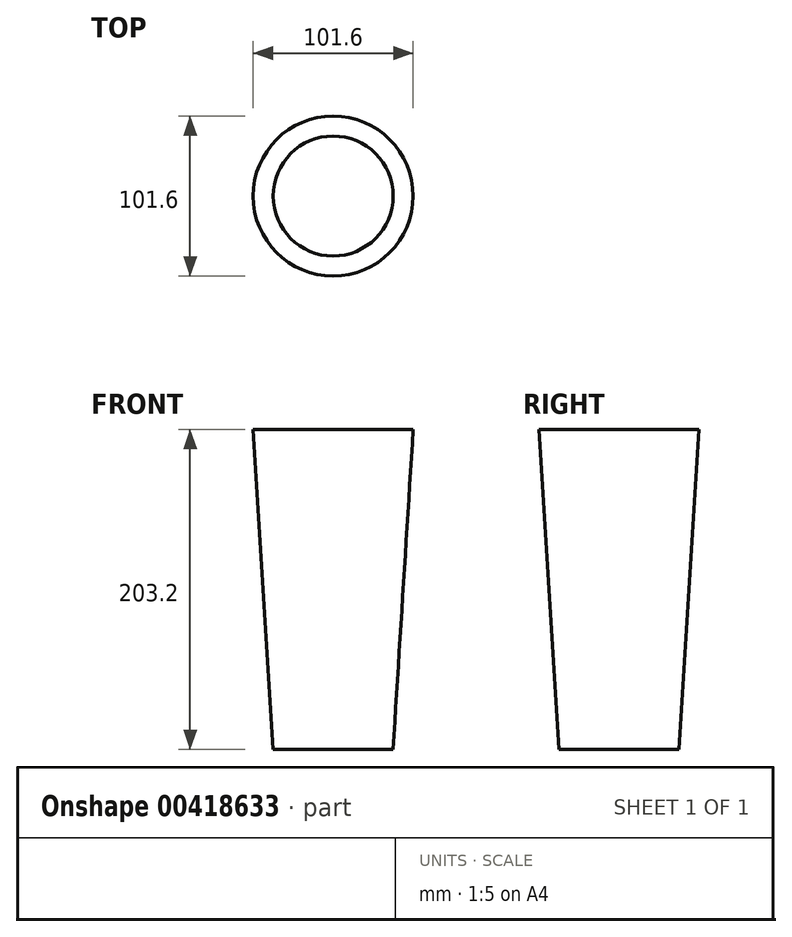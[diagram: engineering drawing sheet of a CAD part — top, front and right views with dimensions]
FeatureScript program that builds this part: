
annotation { "Feature Type Name" : "Feature", "Feature Type Description" : "" }
export const myFeature = defineFeature(function(context is Context, id is Id, definition is map)
    precondition{}
    {
        {
            var Q0;
            Q0=qCreatedBy(makeId("Front.planeOp"),FACE);
            var sketch = newSketch(context, id + "F0", { "sketchPlane" : qUnion([Q0])});
            skLineSegment(sketch, "E0", {"start": v(0, 0) * mm, "end": v(-50.8, 0) * mm, "construction": true});
            skLineSegment(sketch, "E1", {"start": v(-38.1, -203.2) * mm, "end": v(0, -812.8) * mm, "construction": true});
            skLineSegment(sketch, "E2", {"start": v(-38.1, -203.2) * mm, "end": v(0, -203.2) * mm, "construction": true});
            skLineSegment(sketch, "E3", {"start": v(0, -1245.03) * mm, "end": v(0, 0) * mm, "construction": true});
            skLineSegment(sketch, "E4", {"start": v(-50.8, 0) * mm, "end": v(-38.1, -203.2) * mm});
            skLineSegment(sketch, "E5", {"start": v(-50.8, 0) * mm, "end": v(-38.1, -203.2) * mm, "construction": true});
            skSolve(sketch);
        }
        {
            var Q0;
            Q0 = qBodyType(qCreatedBy(id + "F0" ,EDGE), BodyType.WIRE);
            var Q1;
            Q1=sQuery(id+"F0.wireOp",EDGE,"E3");
            revolve(context, id + "F1", {"bodyType" : ExtendedToolBodyType.SURFACE, "surfaceEntities" : qUnion([Q0]), "axis" : qUnion([Q1]), "revolveType" : RevolveType.FULL});
        }
    });
